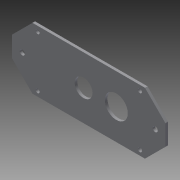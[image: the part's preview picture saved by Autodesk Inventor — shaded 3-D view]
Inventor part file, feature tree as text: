
AUTODESK INVENTOR PART (.ipt)
format: ipt  version: 2015 SP1 (Build 190203100, 203)  size: 152,576 bytes
history: native  units: in
note: dims shown in document units (in); Inventor stores cm internally (conversion verified against a paired STEP export)
features: extrude x4, sketch x4, projected_geometry x3
ambient origin geometry x8: Origin, YZ Plane, XZ Plane, XY Plane, X Axis, Y Axis, Z Axis, Center Point
bodies: Solid1 (feature_tree)
feature tree (11):
  extrude  "Extrusion1"  Depth=3.0in
  extrude  "Extrusion2"  Depth=0.125in
  extrude  "Extrusion3"  Depth=2.75in
  extrude  "Extrusion4"  Depth=0.125in
  sketch  "Sketch1"  dims[d0=5.5in d1=3.0in]
  sketch  "Sketch2"  dims[d2=0.125in d3=0.0in d4=0.25in]
  projected_geometry  "Projected Loop1"
  sketch  "Sketch3"  dims[d5=0.25in d6=2.75in]
  projected_geometry  "Projected Loop2"
  sketch  "Sketch4"  dims[d7=0.25in d8=5.25in d9=0.25in d10=5.25in d11=2.75in d12=2.5in d13=1.5in d14=1.5in d15=4.1in d16=0.2in d17=0.2in d18=0.2in d19=0.2in d20=0.875in d21=1.125in d22=0.125in d23=0.0in d24=1.0in d25=1.0in d26=1.0in d27=1.0in d28=1.0in d29=1.0in d30=0.125in d31=0.0in d32=0.25in d33=0.5in d34=1.5in d35=0.25in d36=6.0in d37=1.5in d38=0.125in d39=0.0in]
  projected_geometry  "Projected Loop3"
